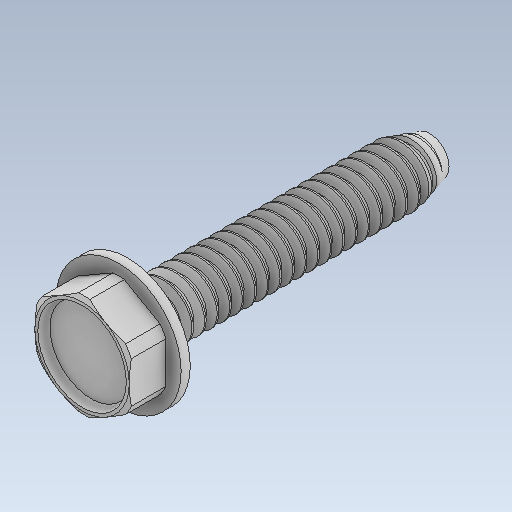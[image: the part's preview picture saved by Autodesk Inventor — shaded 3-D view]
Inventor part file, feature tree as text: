
AUTODESK INVENTOR PART (.ipt)
format: ipt  version: 2020.2 (Build 242310000, 310)  size: 692,736 bytes
history: native  units: in
note: dims shown in document units (in); Inventor stores cm internally (conversion verified against a paired STEP export)
features: chamfer x1
ambient origin geometry x8: Origin, YZ Plane, XZ Plane, XY Plane, X Axis, Y Axis, Z Axis, Center Point
bodies: Solid1 (feature_tree)
feature tree (1):
  chamfer  "Chamfer1"  [1 undecoded]
note: 1 required parameter value undecoded (feature->parameter linkage not recoverable at this tier; creation-order binding heuristic only, values carry confidence <= 0.55)
